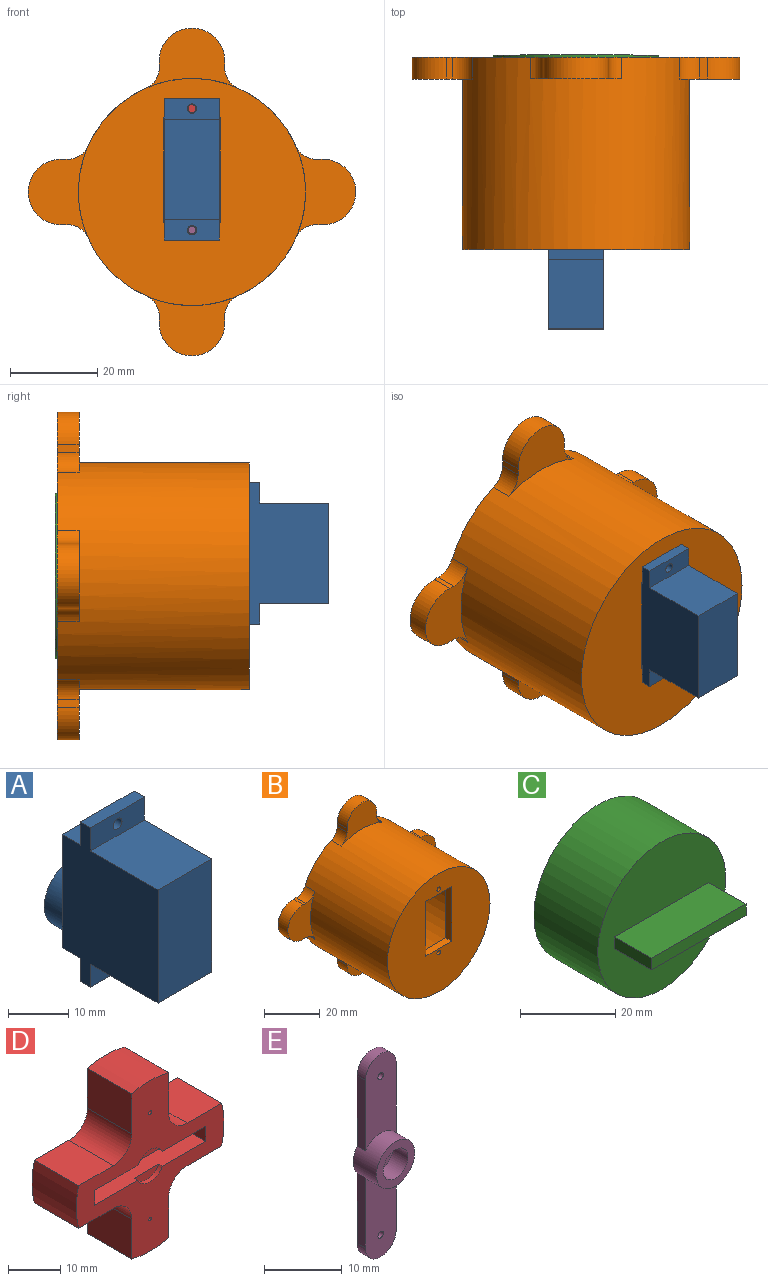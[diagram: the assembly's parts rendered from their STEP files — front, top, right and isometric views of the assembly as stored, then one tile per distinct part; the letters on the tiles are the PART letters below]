
ASSEMBLY  parts=5 mates=4
PART A: 22 faces, bbox 12.6x29.2x32.4 mm
  f0: plane 16.7x12.6mm, normal (0,1,0), area 148.1mm2, adj f3,f4,f6,f18
  f1: plane 6.3x6.3mm, normal (0,1,0), area 8.5mm2, adj f2,f4,f18
  f2: plane 12.6x4.3mm, normal (0,0,-1), area 54.2mm2, adj f1,f4,f6,f9,f13
  f3: plane 12.6x4.3mm, normal (0,0,1), area 54.2mm2, adj f0,f4,f6,f11
  f4: plane 32.4x22.5mm, normal (-1,0,0), area 540.1mm2, adj f0,f1,f2,f3,f5,f7,f8,f10
  f5: plane 15.8x12.6mm, normal (0,0,-1), area 199.1mm2, adj f4,f6,f8,f14
  f6: plane 32.4x22.5mm, normal (1,0,0), area 540.1mm2, adj f0,f2,f3,f5,f7,f8,f9,f10
  f7: plane 15.8x12.6mm, normal (0,0,1), area 199.1mm2, adj f4,f6,f8,f12
  f8: plane 23x12.6mm, normal (0,-1,0), area 289.8mm2, adj f4,f5,f6,f7
  f9: plane 6.3x6.3mm, normal (0,1,0), area 8.5mm2, adj f2,f6,f18
  f10: plane 12.6x2.4mm, normal (0,0,1), area 30.2mm2, adj f4,f6,f11,f12
  f11: plane 12.6x4.7mm, normal (0,1,0), area 55.8mm2, adj f3,f4,f6,f10,f17
  f12: plane 12.6x4.7mm, normal (0,-1,0), area 55.8mm2, adj f4,f6,f7,f10,f17
  f13: plane 12.6x4.7mm, normal (0,1,0), area 55.8mm2, adj f2,f4,f6,f15,f16
  f14: plane 12.6x4.7mm, normal (0,-1,0), area 55.8mm2, adj f4,f5,f6,f15,f16
  f15: plane 12.6x2.4mm, normal (0,0,-1), area 30.2mm2, adj f4,f6,f13,f14
  f16: cylinder r=1.05mm len=2.4mm, axis (0,-1,0), area 15.8mm2, adj f13,f14
  f17: cylinder r=1.05mm len=2.4mm, axis (0,-1,0), area 15.8mm2, adj f11,f12
  f18: cylinder r=6.3mm len=12.6mm, axis (0,-1,0), area 166.3mm2, adj f0,f1,f9,f19
  f19: plane 12.6x12.6mm, normal (0,1,0), area 108.1mm2, adj f18,f20
  f20: cylinder r=2.3mm len=4.6mm, axis (0,-1,0), area 36.1mm2, adj f19,f21
  f21: plane 4.6x4.6mm, normal (0,1,0), area 16.6mm2, adj f20
PART B: 44 faces, bbox 75x44x75 mm
  f0: cylinder r=26mm len=52mm, axis (0,1,0), area 6756.4mm2, adj f1,f2,f9,f13,f17,f21,f36,f37
  f1: plane 52x52mm, normal (0,-1,0), area 1806.6mm2, adj f0,f22,f23,f24,f25,f26,f27
  f2: plane 75x75mm, normal (0,1,0), area 713.5mm2, adj f0,f3,f5,f6,f7,f8,f10,f11
  f3: cylinder r=23mm len=46mm, axis (0,1,0), area 5925mm2, adj f2,f4
  f4: plane 46x46mm, normal (0,1,0), area 1344.8mm2, adj f3,f22,f23,f24,f25,f26,f27
  f5: plane 5x1.19mm, normal (0,0,1), area 6mm2, adj f2,f6,f9,f43
  f6: plane 5x0.01mm, normal (-1,0,0), area 0.1mm2, adj f2,f5,f7,f9
  f7: cylinder r=7.5mm len=15mm, axis (0,1,0), area 122.2mm2, adj f2,f6,f8,f9
  f8: plane 5x1.19mm, normal (0,0,-1), area 5.9mm2, adj f2,f7,f9,f42
  f9: plane 20.96x13.71mm, normal (0,-1,0), area 157.9mm2, adj f0,f5,f6,f7,f8,f42,f43
  f10: plane 5x1.63mm, normal (1,0,0), area 8.2mm2, adj f2,f11,f13,f40
  f11: cylinder r=7.5mm len=15mm, axis (0,1,0), area 117.8mm2, adj f2,f10,f12,f13
  f12: plane 5x1.63mm, normal (-1,0,0), area 8.2mm2, adj f2,f11,f13,f41
  f13: plane 20.97x13.71mm, normal (0,-1,0), area 158mm2, adj f0,f10,f11,f12,f40,f41
  f14: plane 5x1.63mm, normal (-1,0,0), area 8.2mm2, adj f2,f15,f17,f38
  f15: cylinder r=7.5mm len=15mm, axis (0,1,0), area 117.8mm2, adj f2,f14,f16,f17
  f16: plane 5x1.63mm, normal (1,0,0), area 8.2mm2, adj f2,f15,f17,f39
  f17: plane 20.97x13.71mm, normal (0,-1,0), area 158mm2, adj f0,f14,f15,f16,f38,f39
  f18: cylinder r=7.5mm len=15mm, axis (0,1,0), area 120mm2, adj f2,f19,f20,f21
  f19: plane 5x1.63mm, normal (0,0,1), area 8.2mm2, adj f2,f18,f21,f36
  f20: plane 5x1.19mm, normal (0,0,-1), area 5.9mm2, adj f2,f18,f21,f37
  f21: plane 20.96x13.71mm, normal (0,-1,0), area 157.9mm2, adj f0,f18,f19,f20,f36,f37
  f22: plane 24x3mm, normal (1,0,0), area 72mm2, adj f1,f4,f23,f25
  f23: plane 13x3mm, normal (0,0,1), area 39mm2, adj f1,f4,f22,f24
  f24: plane 24x3mm, normal (-1,0,0), area 72mm2, adj f1,f4,f23,f25
  f25: plane 13x3mm, normal (0,0,-1), area 39mm2, adj f1,f4,f22,f24
  f26: cylinder r=0.9mm len=3mm, axis (0,-1,0), area 17mm2, adj f1,f4
  f27: cylinder r=0.9mm len=3mm, axis (0,-1,0), area 17mm2, adj f1,f4
  f28: cylinder r=5.5mm len=11mm, axis (0,1,0), area 69.1mm2, adj f2,f29
  f29: plane 11x11mm, normal (0,1,0), area 95mm2, adj f28
  f30: cylinder r=5.5mm len=11mm, axis (0,1,0), area 69.1mm2, adj f2,f31
  f31: plane 11x11mm, normal (0,1,0), area 95mm2, adj f30
  f32: cylinder r=5.5mm len=11mm, axis (0,1,0), area 69.1mm2, adj f2,f33
  f33: plane 11x11mm, normal (0,1,0), area 95mm2, adj f32
  f34: cylinder r=5.5mm len=11mm, axis (0,1,0), area 69.1mm2, adj f2,f35
  f35: plane 11x11mm, normal (0,1,0), area 95mm2, adj f34
  f36: cylinder r=5mm len=5mm, axis (0,1,0), area 28.9mm2, adj f0,f2,f19,f21
  f37: cylinder r=5mm len=5mm, axis (0,1,0), area 28.9mm2, adj f0,f2,f20,f21
  f38: cylinder r=5mm len=5mm, axis (0,1,0), area 28.9mm2, adj f0,f2,f14,f17
  f39: cylinder r=5mm len=5mm, axis (0,1,0), area 28.9mm2, adj f0,f2,f16,f17
  f40: cylinder r=5mm len=5mm, axis (0,1,0), area 28.9mm2, adj f0,f2,f10,f13
  f41: cylinder r=5mm len=5mm, axis (0,1,0), area 28.9mm2, adj f0,f2,f12,f13
  f42: cylinder r=5mm len=5mm, axis (0,1,0), area 28.9mm2, adj f0,f2,f8,f9
  f43: cylinder r=5mm len=5mm, axis (0,1,0), area 28.9mm2, adj f0,f2,f5,f9
PART C: 8 faces, bbox 38x30x38 mm
  f0: plane 38x38mm, normal (0,-1,0), area 1050.1mm2, adj f1,f3,f4,f5,f6
  f1: cylinder r=19mm len=38mm, axis (0,1,0), area 2268.2mm2, adj f0,f2
  f2: plane 38x38mm, normal (0,1,0), area 1134.1mm2, adj f1
  f3: plane 11x3mm, normal (-1,0,0), area 33mm2, adj f0,f4,f6,f7
  f4: plane 28x11mm, normal (0,0,-1), area 308mm2, adj f0,f3,f5,f7
  f5: plane 11x3mm, normal (1,0,0), area 33mm2, adj f0,f4,f6,f7
  f6: plane 28x11mm, normal (0,0,1), area 308mm2, adj f0,f3,f5,f7
  f7: plane 28x3mm, normal (0,-1,0), area 84mm2, adj f3,f4,f5,f6
PART D: 28 faces, bbox 40x12x40 mm
  f0: plane 40x40mm, normal (0,-1,0), area 588.1mm2, adj f2,f3,f4,f5,f6,f7,f8,f9
  f1: plane 40x40mm, normal (0,1,0), area 607mm2, adj f2,f3,f4,f5,f6,f7,f8,f9
  f2: cylinder r=20mm len=12mm, axis (0,1,0), area 121.3mm2, adj f0,f1,f16,f22
  f3: cylinder r=20mm len=12mm, axis (0,1,0), area 121.3mm2, adj f0,f1,f20,f23
  f4: cylinder r=20mm len=12mm, axis (0,1,0), area 121.3mm2, adj f0,f1,f18,f21
  f5: cylinder r=20mm len=12mm, axis (0,1,0), area 121.3mm2, adj f0,f1,f17,f19
  f6: plane 12x3.5mm, normal (1,0,0), area 42mm2, adj f0,f1,f7,f9
  f7: plane 30x12mm, normal (0,0,1), area 353.4mm2, adj f0,f1,f6,f8,f14,f15
  f8: plane 12x3.5mm, normal (-1,0,0), area 42mm2, adj f0,f1,f7,f9
  f9: plane 30x12mm, normal (0,0,-1), area 353.4mm2, adj f0,f1,f6,f8,f12,f13
  f10: cylinder r=0.4mm len=12mm, axis (0,-1,0), area 30.2mm2, adj f0,f1
  f11: cylinder r=0.4mm len=12mm, axis (0,-1,0), area 30.2mm2, adj f0,f1
  f12: plane 6.63x2mm, normal (0,-1,0), area 9.5mm2, adj f9,f13
  f13: cylinder r=3.75mm len=6.63mm, axis (0,-1,0), area 8.1mm2, adj f0,f9,f12
  f14: cylinder r=3.75mm len=6.63mm, axis (0,-1,0), area 8.1mm2, adj f0,f7,f15
  f15: plane 6.63x2mm, normal (0,-1,0), area 9.5mm2, adj f7,f14
  f16: plane 12x9.37mm, normal (-1,0,0), area 112.4mm2, adj f0,f1,f2,f27
  f17: plane 12x9.37mm, normal (0,0,-1), area 112.4mm2, adj f0,f1,f5,f27
  f18: plane 12x9.37mm, normal (-1,0,0), area 112.4mm2, adj f0,f1,f4,f26
  f19: plane 12x9.37mm, normal (0,0,1), area 112.4mm2, adj f0,f1,f5,f26
  f20: plane 12x9.37mm, normal (0,0,1), area 112.4mm2, adj f0,f1,f3,f25
  f21: plane 12x9.37mm, normal (1,0,0), area 112.4mm2, adj f0,f1,f4,f25
  f22: plane 12x9.37mm, normal (1,0,0), area 112.4mm2, adj f0,f1,f2,f24
  f23: plane 12x9.37mm, normal (0,0,-1), area 112.4mm2, adj f0,f1,f3,f24
  f24: cylinder r=5mm len=12mm, axis (0,-1,0), area 94.2mm2, adj f0,f1,f22,f23
  f25: cylinder r=5mm len=12mm, axis (0,1,0), area 94.2mm2, adj f0,f1,f20,f21
  f26: cylinder r=5mm len=12mm, axis (0,1,0), area 94.2mm2, adj f0,f1,f18,f19
  f27: cylinder r=5mm len=12mm, axis (0,-1,0), area 94.2mm2, adj f0,f1,f16,f17
PART E: 15 faces, bbox 7x4.2x32 mm
  f0: cylinder r=3.5mm len=7mm, axis (0,-1,0), area 72.9mm2, adj f1,f2,f4,f5,f6,f7,f8,f9
  f1: plane 32x7mm, normal (0,1,0), area 174.9mm2, adj f0,f3,f5,f6,f8,f9,f10,f11
  f2: plane 7x7mm, normal (0,-1,0), area 22.6mm2, adj f0,f13
  f3: cylinder r=2.8mm len=5.6mm, axis (0,1,0), area 13.2mm2, adj f1,f4,f5,f6
  f4: plane 13.9x5.6mm, normal (0,-1,0), area 68.2mm2, adj f0,f3,f5,f6,f11
  f5: plane 11.1x1.5mm, normal (1,0,0), area 16.6mm2, adj f0,f1,f3,f4
  f6: plane 11.1x1.5mm, normal (-1,0,0), area 16.6mm2, adj f0,f1,f3,f4
  f7: plane 13.9x5.6mm, normal (0,-1,0), area 68.2mm2, adj f0,f8,f9,f10,f12
  f8: plane 11.1x1.5mm, normal (-1,0,0), area 16.6mm2, adj f0,f1,f7,f10
  f9: plane 11.1x1.5mm, normal (1,0,0), area 16.6mm2, adj f0,f1,f7,f10
  f10: cylinder r=2.8mm len=5.6mm, axis (0,1,0), area 13.2mm2, adj f1,f7,f8,f9
  f11: cylinder r=0.5mm len=1.5mm, axis (0,-1,0), area 4.7mm2, adj f1,f4
  f12: cylinder r=0.5mm len=1.5mm, axis (0,-1,0), area 4.7mm2, adj f1,f7
  f13: cylinder r=2.25mm len=4.5mm, axis (0,-1,0), area 38.2mm2, adj f2,f14
  f14: plane 4.5x4.5mm, normal (0,-1,0), area 15.9mm2, adj f13
PLACE A t=(-13.98,-47.87,23.89)mm
PLACE B t=(-13.98,-8.17,23.89)mm
PLACE C t=(-13.98,-7.67,23.89)mm
PLACE D t=(-13.98,-27.67,23.89)mm
PLACE E t=(-13.98,-43.87,23.89)mm
MATE fastened E.f0 <-> D.f2  axis (0,1,0) through (-13.98,-39.67,23.89)mm
MATE fastened C.f1 <-> D.f2  axis (0,1,0) through (-13.98,-7.67,23.89)mm
MATE fastened A.f18 <-> E.f0  axis (0,1,0) through (-13.98,-41.17,23.89)mm
MATE fastened C.f1 <-> B.f0  axis (0,1,0) through (-13.98,-7.67,23.89)mm
